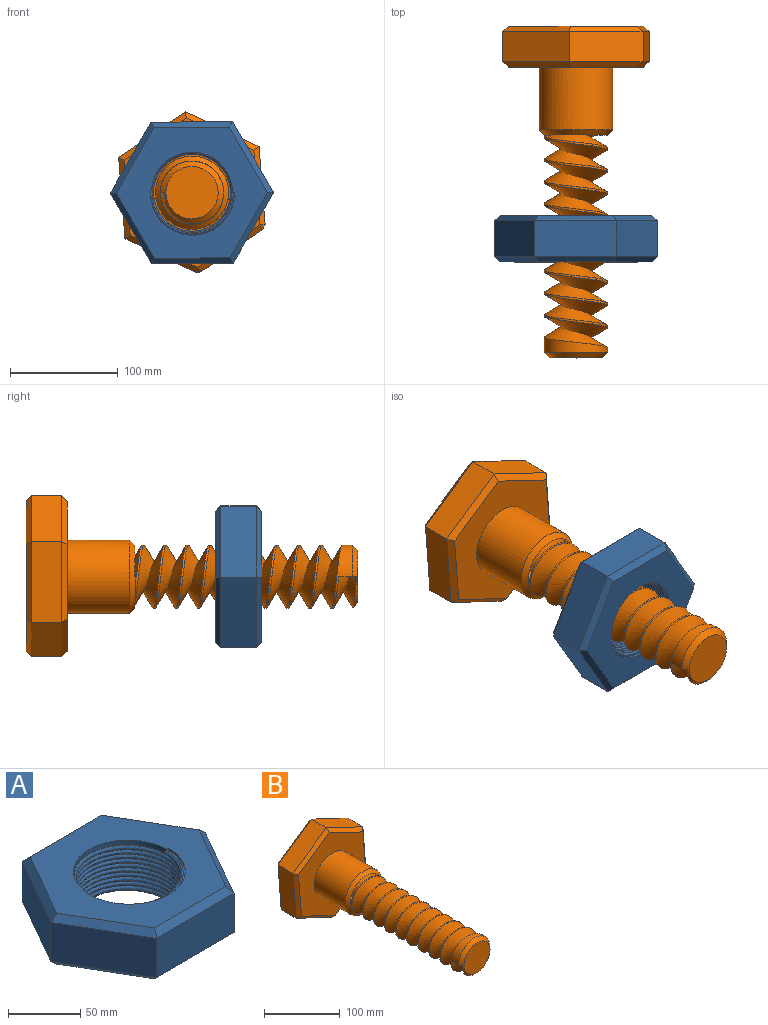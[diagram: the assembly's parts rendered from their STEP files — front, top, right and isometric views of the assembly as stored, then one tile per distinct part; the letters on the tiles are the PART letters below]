
ASSEMBLY  parts=2 mates=1
PART A: 36 faces, bbox 151.9x132x43.2 mm
  f0: plane 3.93x2.03mm, normal (0,1,0), area 6.2mm2, adj f1,f9,f14,f15
  f1: cylinder r=37.76mm len=75.08mm, axis (0,0,-1), area 389.5mm2, adj f0,f9,f16,f18,f19
  f2: plane 65.53x38.32mm, normal (0.86,0.5,0), area 2518.7mm2, adj f3,f8,f24,f35
  f3: plane 75.91x33.18mm, normal (-0.01,1,0), area 2518.7mm2, adj f2,f4,f26,f33
  f4: plane 65.95x37.59mm, normal (-0.87,0.5,0), area 2518.7mm2, adj f3,f5,f28,f31
  f5: plane 65.53x38.32mm, normal (-0.86,-0.5,0), area 2518.7mm2, adj f4,f6,f29,f30
  f6: plane 75.91x33.18mm, normal (0.01,-1,0), area 2518.7mm2, adj f5,f8,f27,f32
  f7: cylinder r=37.76mm len=75.08mm, axis (0,0,-1), area 389.5mm2, adj f10,f12,f21,f22,f23
  f8: plane 65.95x37.59mm, normal (0.87,-0.5,0), area 2518.7mm2, adj f2,f6,f25,f34
  f9: bspline ~88.56x76.69mm, area 213mm2, adj f0,f1,f13,f14,f16,f18
  f10: bspline ~88.56x76.69mm, area 212.4mm2, adj f7,f11,f12,f15,f21,f22
  f11: bspline ~80.33x79.51mm, area 155.5mm2, adj f10,f20,f22
  f12: plane 3.93x2.03mm, normal (0,-1,0), area 6.2mm2, adj f7,f10,f14,f15
  f13: bspline ~79.51x45.9mm, area 180.9mm2, adj f9,f16,f17
  f14: bspline ~85.86x74.35mm, area 5769.6mm2, adj f0,f9,f12,f15
  f15: bspline ~85.86x74.35mm, area 5800.8mm2, adj f0,f10,f12,f14
  f16: plane 2.57x2.03mm, normal (0,-1,0), area 1.9mm2, adj f1,f9,f13,f17,f19
  f17: bspline ~78.16x39.51mm, area 314.3mm2, adj f13,f16,f18,f19
  f18: bspline ~5.77x2.54mm, area 15mm2, adj f1,f9,f17,f19
  f19: plane 140.33x121.93mm, normal (0,0,1), area 8105.1mm2, adj f1,f16,f17,f18,f24,f25,f26,f27
  f20: bspline ~78.14x39.52mm, area 314.3mm2, adj f11,f21,f22,f23
  f21: bspline ~5.77x2.54mm, area 15mm2, adj f7,f10,f20,f23
  f22: plane 2.57x2.03mm, normal (0,1,0), area 1.9mm2, adj f7,f10,f11,f20,f23
  f23: plane 140.33x121.92mm, normal (0,0,-1), area 8104.9mm2, adj f7,f20,f21,f22,f30,f31,f32,f33
  f24: plane 65.56x41.18mm, normal (0.61,0.36,0.71), area 516.4mm2, adj f2,f19,f25,f26
  f25: plane 65.95x40.51mm, normal (0.61,-0.35,0.71), area 516.4mm2, adj f8,f19,f24,f27
  f26: plane 75.91x5.4mm, normal (0,0.71,0.71), area 516.4mm2, adj f3,f19,f24,f28
  f27: plane 75.91x5.4mm, normal (0,-0.71,0.71), area 516.4mm2, adj f6,f19,f25,f29
  f28: plane 65.95x40.51mm, normal (-0.61,0.35,0.71), area 516.4mm2, adj f4,f19,f26,f29
  f29: plane 65.56x41.18mm, normal (-0.61,-0.36,0.71), area 516.4mm2, adj f5,f19,f27,f28
  f30: plane 65.56x41.18mm, normal (-0.61,-0.36,-0.71), area 516.4mm2, adj f5,f23,f31,f32
  f31: plane 65.95x40.51mm, normal (-0.61,0.35,-0.71), area 516.4mm2, adj f4,f23,f30,f33
  f32: plane 75.91x5.4mm, normal (0,-0.71,-0.71), area 516.4mm2, adj f6,f23,f30,f34
  f33: plane 75.91x5.4mm, normal (0,0.71,-0.71), area 516.4mm2, adj f3,f23,f31,f35
  f34: plane 65.95x40.51mm, normal (0.61,-0.35,-0.71), area 516.4mm2, adj f8,f23,f32,f35
  f35: plane 65.56x41.18mm, normal (0.61,0.36,-0.71), area 516.4mm2, adj f2,f23,f33,f34
PART B: 37 faces, bbox 136.1x309.4x149.4 mm
  f0: cone r=28.94mm half-angle=45deg, axis (0,1,0), area 1333.4mm2, adj f1,f10,f14,f17,f18
  f1: plane 23.11x11.91mm, normal (0,1,0), area 10.4mm2, adj f0,f11,f14,f17
  f2: plane 72.38x27.94mm, normal (1,0,0.08), area 2028.6mm2, adj f3,f22,f30,f31
  f3: plane 68.17x32.55mm, normal (0.43,0,0.9), area 2110.5mm2, adj f2,f4,f20,f27
  f4: plane 62.27x42.76mm, normal (-0.57,0,0.82), area 2110.5mm2, adj f3,f5,f19,f23
  f5: plane 75.31x27.94mm, normal (-1,0,-0.08), area 2110.5mm2, adj f4,f6,f21,f28
  f6: plane 65.52x31.29mm, normal (-0.43,0,-0.9), area 2028.6mm2, adj f5,f24,f32,f33
  f7: plane 57.44x39.44mm, normal (0.57,0,-0.82), area 1946.6mm2, adj f25,f30,f33,f36
  f8: plane 138.92x125.74mm, normal (0,-1,0), area 8974.7mm2, adj f10,f19,f20,f21,f22,f24,f25
  f9: plane 138.92x125.74mm, normal (0,1,0), area 12611.5mm2, adj f23,f27,f28,f31,f32,f36
  f10: cylinder r=34.02mm len=68.05mm, axis (0,1,0), area 12489mm2, adj f0,f8
  f11: cylinder r=29.34mm len=201.68mm, axis (0,1,0), area 3194.9mm2, adj f1,f13,f14,f15,f16,f17
  f12: plane 48.53x48.53mm, normal (0,-1,0), area 1849.5mm2, adj f13
  f13: cone r=24.26mm half-angle=45deg, axis (0,1,0), area 1067mm2, adj f11,f12,f15,f16
  f14: plane 18.9x16.37mm, normal (0,0,1), area 154.6mm2, adj f0,f1,f11,f16,f17,f18
  f15: plane 16.66x16.37mm, normal (0,0,-1), area 142.8mm2, adj f11,f13,f16,f17
  f16: bspline ~216.21x61.71mm, area 25255.8mm2, adj f11,f13,f14,f15,f17
  f17: bspline ~216.21x61.71mm, area 25356.7mm2, adj f0,f1,f11,f14,f15,f16,f18
  f18: cylinder r=29.34mm len=58.69mm, axis (0,-1,0), area 1360.4mm2, adj f0,f14,f17
  f19: plane 62.73x45.29mm, normal (-0.4,-0.71,0.58), area 521.6mm2, adj f4,f8,f20,f21
  f20: plane 68.17x35.87mm, normal (0.3,-0.71,0.64), area 521.6mm2, adj f3,f8,f19,f22
  f21: plane 75.31x10.73mm, normal (-0.7,-0.71,-0.06), area 521.6mm2, adj f5,f8,f19,f24
  f22: plane 72.78x10.5mm, normal (0.7,-0.71,0.06), area 511.1mm2, adj f2,f8,f20,f26
  f23: plane 62.73x45.29mm, normal (-0.4,0.71,0.58), area 521.6mm2, adj f4,f9,f27,f28
  f24: plane 67.71x34.61mm, normal (-0.3,-0.71,-0.64), area 511.1mm2, adj f6,f8,f21,f29
  f25: plane 60.31x43.63mm, normal (0.4,-0.71,-0.58), area 500.5mm2, adj f7,f8,f26,f29
  f26: plane 5.08x5.06mm, normal (0.68,-0.65,-0.33), area 17.1mm2, adj f22,f25,f30
  f27: plane 68.17x35.87mm, normal (0.3,0.71,0.64), area 521.6mm2, adj f3,f9,f23,f31
  f28: plane 75.31x10.73mm, normal (-0.7,0.71,-0.06), area 521.6mm2, adj f5,f9,f23,f32
  f29: plane 5.08x5.06mm, normal (0.06,-0.65,-0.75), area 17.1mm2, adj f24,f25,f33
  f30: plane 27.94x4.58mm, normal (0.9,0,-0.43), area 141.9mm2, adj f2,f7,f26,f34
  f31: plane 72.78x10.5mm, normal (0.7,0.71,0.06), area 511.1mm2, adj f2,f9,f27,f34
  f32: plane 67.71x34.61mm, normal (-0.3,0.71,-0.64), area 511.1mm2, adj f6,f9,f28,f35
  f33: plane 27.94x5.06mm, normal (0.08,0,-1), area 141.9mm2, adj f6,f7,f29,f35
  f34: plane 5.08x5.06mm, normal (0.68,0.65,-0.33), area 17.1mm2, adj f30,f31,f36
  f35: plane 5.08x5.06mm, normal (0.06,0.65,-0.75), area 17.1mm2, adj f32,f33,f36
  f36: plane 60.31x43.63mm, normal (0.4,0.71,-0.58), area 500.5mm2, adj f7,f9,f34,f35
PLACE A rot(axis=(1,0,0),90deg) t=(16.83,-178.51,103.16)mm
PLACE B t=(16.83,0,103.16)mm fixed
MATE cylindrical A.f1 <-> B.f0  axis (0,1,0) through (16.83,-175.97,103.16)mm
